# Revit family: Practibox_S_18_modules_saillie_réf_137526_à_137539
name_source: partatom
category: Equipement électrique
revit_build: Autodesk Revit 2018 (Build: 20170223_1515(x64)
units: mm (PartAtom-declared; Revit-internal decimal feet)

## family parameters
Basée sur le plan de construction = Non
Configuration du panneau = Deux colonnes, circuits au sein
Cote de connecteur circulaire = Utiliser le diamètre
Couper avec des vides une fois chargée = Non
Numéro OmniClass = 23.80.30.11.17
Partagée = Non
Point de calcul de pièce = Non
Titre OmniClass = Distribution Boards and Control Panels
Toujours verticalement = Oui
Type d'élément = Tableau de raccordement

## types (8) — shared parameters
Bornier T = 27 départs Icc 10kA
Conditions Générale d'Utilisation = https://export.legrand.com
Fabricant = "Legrand"
Largeur = 436 mm  [stored 1.43045 ft]
URL = www.legrand.com
profondeur = 320 mm  [stored 1.04987 ft]

## per-type parameters (varying)
| type | 1R | 2R | 3R | 4R | Hauteur | Ina | porte B 1 r | porte B 2 r | porte B 3 r | porte B 4 r | porte T 1 r | porte T 2 r | porte T 3 r | porte T 4 r | porte blanche | porte transparente | taille |
| Practibox_S_18_modules_saillie_137526 | Oui | Non | Non | Non | 236 mm | 63A | Oui | Non | Non | Non | Non | Non | Non | Non | Oui | Non | 1 rangée |
| Practibox_S_18_modules_saillie_137536 | Oui | Non | Non | Non | 236 mm | 63A | Non | Non | Non | Non | Oui | Non | Non | Non | Non | Oui | 1 rangée |
| Practibox_S_36_modules_saillie_137527 | Non | Oui | Non | Non | 386 mm  [stored 1.2664 ft] | 90A | Non | Oui | Non | Non | Non | Non | Non | Non | Oui | Non | 2 rangée |
| Practibox_S_36_modules_saillie_137537 | Non | Oui | Non | Non | 386 mm  [stored 1.2664 ft] | 90A | Non | Non | Non | Non | Non | Oui | Non | Non | Non | Oui | 2 rangée |
| Practibox_S_54_modules_saillie_137538 | Non | Non | Oui | Non | 386 mm  [stored 1.2664 ft] | 90A | Non | Non | Non | Non | Non | Non | Oui | Non | Non | Oui | 3 rangée |
| Practibox_S_54_modules_saillie_137528 | Non | Non | Oui | Non | 386 mm  [stored 1.2664 ft] | 90A | Non | Non | Oui | Non | Non | Non | Non | Non | Oui | Non | 3 rangée |
| Practibox_S_72_modules_saillie_137529 | Non | Non | Non | Oui | 386 mm  [stored 1.2664 ft] | 90A | Non | Non | Non | Oui | Non | Non | Non | Non | Oui | Non | 4 rangée |
| Practibox_S_72_modules_saillie_137539 | Non | Non | Non | Oui | 386 mm  [stored 1.2664 ft] | 90A | Non | Non | Non | Non | Non | Non | Non | Oui | Non | Oui | 4 rangée |

note: column(s) folded — value = type name in every type: Description

note: [stored X ft] marks values corroborated as IEEE doubles in the binary element streams (Revit-internal decimal feet)
